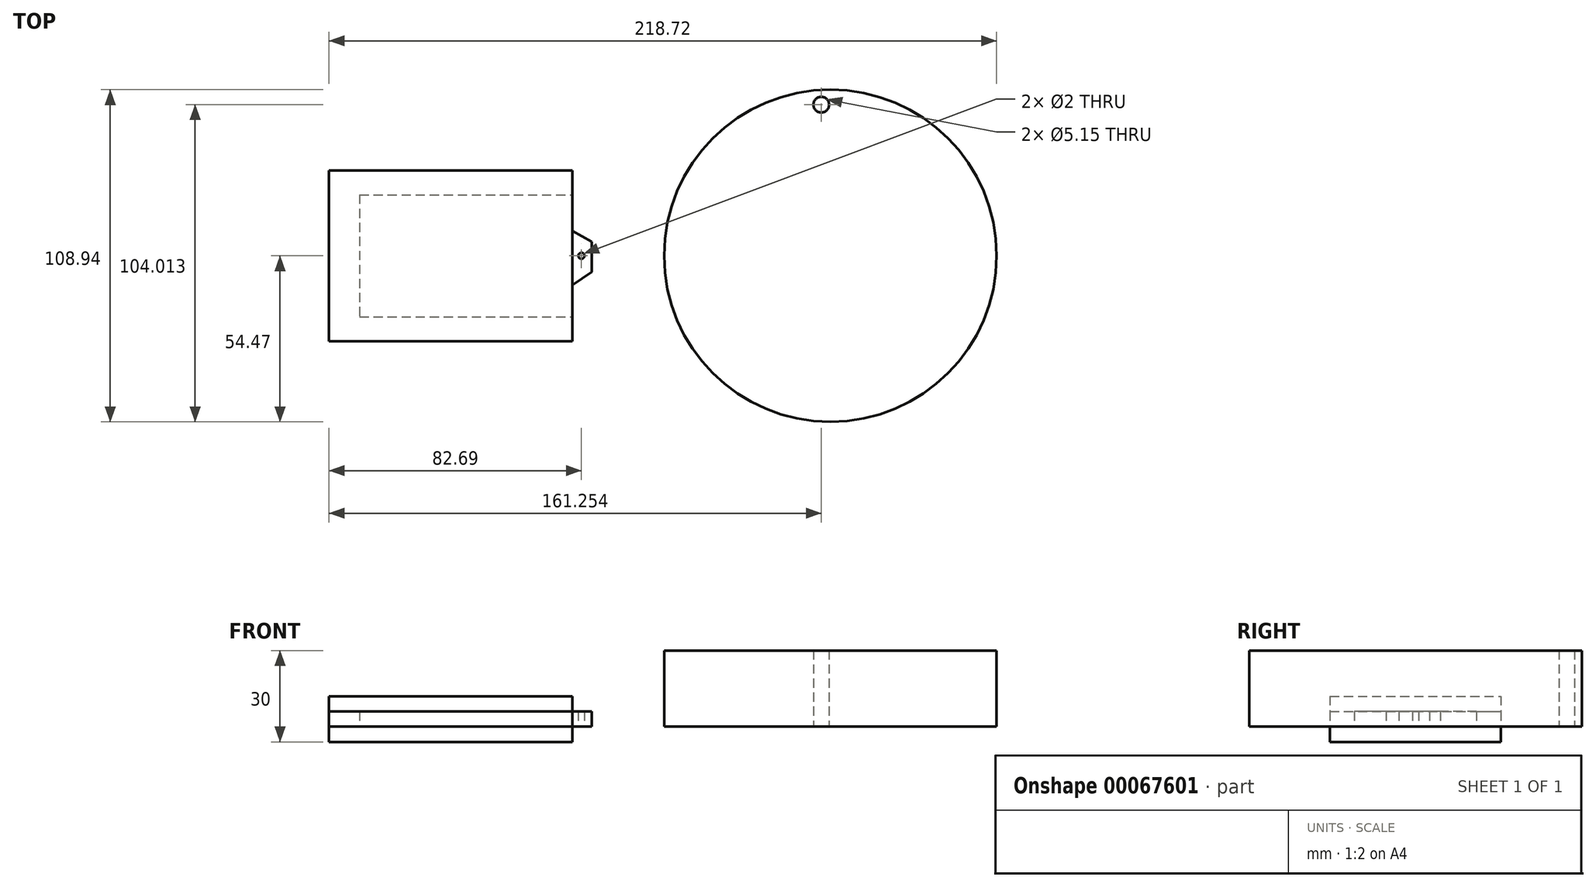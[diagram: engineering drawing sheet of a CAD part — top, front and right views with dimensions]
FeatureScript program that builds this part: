
annotation { "Feature Type Name" : "Feature", "Feature Type Description" : "" }
export const myFeature = defineFeature(function(context is Context, id is Id, definition is map)
    precondition{}
    {
        {
            var Q0;
            Q0=qCreatedBy(makeId("Top.planeOp"),FACE);
            var sketch = newSketch(context, id + "F0", { "sketchPlane" : qUnion([Q0])});
            skLineSegment(sketch, "E0.bottom", {"start": v(-31.15, 20) * mm, "end": v(38.6, 20) * mm});
            skLineSegment(sketch, "E0.top", {"start": v(-31.15, -20) * mm, "end": v(38.6, -20) * mm});
            skLineSegment(sketch, "E0.left", {"start": v(-31.15, 20) * mm, "end": v(-31.15, -20) * mm});
            skLineSegment(sketch, "E0.right", {"start": v(38.6, 20) * mm, "end": v(38.6, -20) * mm});
            skLineSegment(sketch, "E1", {"start": v(38.6, 20) * mm, "end": v(38.6, 28) * mm});
            skLineSegment(sketch, "E2", {"start": v(38.6, 28) * mm, "end": v(-41.15, 28) * mm});
            skLineSegment(sketch, "E3", {"start": v(-41.15, 28) * mm, "end": v(-41.15, -28) * mm});
            skLineSegment(sketch, "E4", {"start": v(-41.15, -28) * mm, "end": v(38.6, -28) * mm});
            skLineSegment(sketch, "E5", {"start": v(38.6, -28) * mm, "end": v(38.6, -20) * mm});
            skLineSegment(sketch, "E6", {"start": v(11, 0) * mm, "end": v(38.6, 0) * mm, "construction": true});
            skLineSegment(sketch, "E7", {"start": v(38.6, 8.17) * mm, "end": v(44.98, 4.61) * mm});
            skLineSegment(sketch, "E8", {"start": v(44.98, 4.61) * mm, "end": v(44.98, -5.37) * mm});
            skLineSegment(sketch, "E9", {"start": v(44.98, -5.37) * mm, "end": v(38.6, -9.62) * mm});
            skCircle(sketch, "E10", {"center": v(41.54, 0) * mm, "radius": 1 * mm});
            skSolve(sketch);
        }
        {
            var Q0;
            Q0=makeQuery(id+"F0.imprint","IMPRINT",FACE,{"disambiguationData":[TD([[makeQuery(id+"F0.imprint","IMPRINT",EDGE,{"derivedFrom":sQuery(id+"F0.wireOp",EDGE,"E0.bottom")}),-1.0]])]});
            var Q1;
            {var subQ1=sQuery(id+"F0.wireOp",EDGE,"E7");Q1=makeQuery(id+"F0.imprint","IMPRINT",FACE,{"disambiguationData":[TD([[makeQuery(id+"F0.imprint","IMPRINT",EDGE,{"derivedFrom":subQ1}),-1.0]])]});}
            extrude(context, id + "F1", {"entities" : qUnion([Q0, Q1]), "depth" : 5 * mm});
        }
        {
            var Q0;
            Q0=makeQuery(id+"F0.imprint","IMPRINT",FACE,{"disambiguationData":[TD([[makeQuery(id+"F0.imprint","IMPRINT",EDGE,{"derivedFrom":sQuery(id+"F0.wireOp",EDGE,"E0.bottom")}),1.0]])]});
            extrude(context, id + "F2", {"entities" : qUnion([Q0]), "depth" : 5 * mm});
        }
        {
            var Q0;
            Q0=makeQuery(id+"F2.opExtrude","CAP_FACE",FACE,{"disambiguationData":[OSD([sQuery(id+"F0.wireOp",EDGE,"E0.bottom"),sQuery(id+"F0.wireOp",EDGE,"E0.top"),sQuery(id+"F0.wireOp",EDGE,"E0.left"),sQuery(id+"F0.wireOp",EDGE,"E1"),sQuery(id+"F0.wireOp",EDGE,"E2"),sQuery(id+"F0.wireOp",EDGE,"E3"),sQuery(id+"F0.wireOp",EDGE,"E4"),sQuery(id+"F0.wireOp",EDGE,"E5")])],"isStart":false});
            var sketch = newSketch(context, id + "F3", { "sketchPlane" : qUnion([Q0])});
            skLineSegment(sketch, "E11.0", {"start": v(38.6, 28) * mm, "end": v(-41.15, 28) * mm});
            skLineSegment(sketch, "E12.0", {"start": v(-41.15, 28) * mm, "end": v(-41.15, -28) * mm});
            skLineSegment(sketch, "E13.0", {"start": v(-41.15, -28) * mm, "end": v(38.6, -28) * mm});
            skLineSegment(sketch, "E14.0", {"start": v(38.6, 20) * mm, "end": v(38.6, 28) * mm});
            skLineSegment(sketch, "E15.0", {"start": v(38.6, 20) * mm, "end": v(38.6, -20) * mm});
            skLineSegment(sketch, "E16.0", {"start": v(38.6, -28) * mm, "end": v(38.6, -20) * mm});
            skSolve(sketch);
        }
        {
            var Q0;
            Q0 = qSketchRegion(id + "F3", true);
            extrude(context, id + "F4", {"entities" : qUnion([Q0]), "depth" : 5 * mm});
        }
        {
            var Q0;
            Q0=makeQuery(id+"F2.opExtrude","CAP_FACE",FACE,{"disambiguationData":[OSD([sQuery(id+"F0.wireOp",EDGE,"E0.bottom"),sQuery(id+"F0.wireOp",EDGE,"E0.top"),sQuery(id+"F0.wireOp",EDGE,"E0.left"),sQuery(id+"F0.wireOp",EDGE,"E1"),sQuery(id+"F0.wireOp",EDGE,"E2"),sQuery(id+"F0.wireOp",EDGE,"E3"),sQuery(id+"F0.wireOp",EDGE,"E4"),sQuery(id+"F0.wireOp",EDGE,"E5")])],"isStart":true});
            var sketch = newSketch(context, id + "F5", { "sketchPlane" : qUnion([Q0])});
            skLineSegment(sketch, "E17.0", {"start": v(-41.15, -28) * mm, "end": v(-41.15, 28) * mm});
            skLineSegment(sketch, "E17.1", {"start": v(38.6, -28) * mm, "end": v(-41.15, -28) * mm});
            skLineSegment(sketch, "E17.2", {"start": v(38.6, -20) * mm, "end": v(38.6, -28) * mm});
            skLineSegment(sketch, "E17.3", {"start": v(38.6, -20) * mm, "end": v(38.6, 20) * mm});
            skLineSegment(sketch, "E17.4", {"start": v(38.6, 28) * mm, "end": v(38.6, 20) * mm});
            skLineSegment(sketch, "E17.5", {"start": v(-41.15, 28) * mm, "end": v(38.6, 28) * mm});
            skSolve(sketch);
        }
        {
            var Q0;
            Q0 = qSketchRegion(id + "F5", true);
            extrude(context, id + "F6", {"entities" : qUnion([Q0]), "depth" : 5 * mm});
        }
        {
            var Q0;
            Q0=qCreatedBy(makeId("Top.planeOp"),FACE);
            var sketch = newSketch(context, id + "F7", { "sketchPlane" : qUnion([Q0])});
            skCircle(sketch, "E18", {"center": v(123.1, 0) * mm, "radius": 54.47 * mm});
            skCircle(sketch, "E19", {"center": v(120.1, 49.54) * mm, "radius": 2.58 * mm});
            skSolve(sketch);
        }
        {
            var Q0;
            Q0 = qSketchRegion(id + "F7", true);
            var Q1;
            Q1=makeQuery(id+"F7.imprint","IMPRINT",FACE,{"disambiguationData":[TD([[makeQuery(id+"F7.imprint","IMPRINT",EDGE,{"derivedFrom":sQuery(id+"F7.wireOp",EDGE,"E18")}),1.0]])]});
            extrude(context, id + "F8", {"entities" : qUnion([Q0, Q1]), "depth" : 25 * mm});
        }
    });
